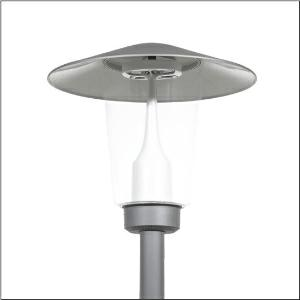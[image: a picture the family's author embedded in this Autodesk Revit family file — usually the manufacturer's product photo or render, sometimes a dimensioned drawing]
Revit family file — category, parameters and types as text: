
# Revit family: pilzleuchte_iq___p1_0a_5xa5235nf14hp_8191
name_source: partatom
category: Lighting Fixtures
units: mm (PartAtom-declared; Revit-internal decimal feet)

## family parameters
Cut with Voids When Loaded = No
Host = Face
Light Source = No
Part Type = Normal
Room Calculation Point = No
Round Connector Dimension = Use Diameter
Shared = No

## types (1)
- --- (1 x LED, 4250 lm, 33.6 W, 2700K)
    Apparent Load = 34 VA
    CIE Flux Codes = 35 64 90 96 100
    Color Rendering = 70
    Color Temperature = 2700K
    Default Elevation = 1800 mm
    Description = Mushroom Luminaire iQ, mast luminaire, Module 540 iQ-SR, primary light control with 3 zone facetted reflector, of plastic, silver coated, highly specular, structured, primary optical cover: cover, of PMMA, transparent, light distribution: P1.0a, light emission: direct distribution, primary light characteristic: strongly asymmetric, installation type: post-top, LED, High Power LED, rated luminous flux: 4.250lm, luminous efficacy: 127lm/W, light colour: 727, colour temperature: 2700K, control gear: ECG iQ, control: presetting dimming logarithmic, Street-Remote, Auto-Match, Temp-Guard, Lumen-Switch, Night-Set, Smart-Wire, Light-Fading, Desk-Remote (wireless, voltage-free reading and setting of iQ features in the workshop via application-optimized NFC function/RFID function), optimised constant luminous flux control (CLO 2.0), with terminal, 6-pole, max. 2.5mm², mains connection: 230..240V, AC, 50/60Hz, start of lifetime: 34W, end of service life: 36W, reduction: 15W, luminaire housing, upper part, of glass-fibre reinforced polyester, coated, Siteco® metallic grey (DB 702S), diameter: 650mm, height: 586mm, spigot size: d x l = 76 x 70mm (post-top) | with reducer (optional accessory) 60 x 70mm, post-top mast mounting element, of diecast aluminium, coated, Siteco® metallic grey (DB 702S), Module 540 iQ-SR, traffic white (RAL 9016), equipment: Power, protection rating (complete): IP65, insulation class (complete): insulation class II (safety insulation), certification: CE, ENEC, VDE, packaging unit: 1 piece

Light Distribution: P1.0a
    Height = 586 mm
    Lamp = 1 x LED
    Lamp Light Flux = 4250 lm
    Lamp Power = 33.6 W
    Lamp count = 1
    Length = 650 mm
    Luminous efficacy = 126 lm/W
    Manufacturer = Siteco
    ModVariant = No
    Model = 5XA5235NF14HP
    Number of Poles = 1
    OnlyDefault = Yes
    Power Factor = 1
    Product Name = Pilzleuchte iQ | P1.0a
    Product group = mast luminaire | pylon top
    ProductGroupID = 6100
    Protection Class = Protection class II
    Protection Degree = IP 65
    RLX_Detail_Level = 1
    RLX_Emergency_Light_Flux = 0 lm
    RLX_Emergency_Type = 0
    RLX_Emergency_Type_DB = No
    RlxData = <blob elided: 51913 chars, md5=ce1a9bcf>
    Socket = socket
    Standby Power = 0 W
    System Light Flux = 4250 lm
    System Power = 34 W
    Type Comments = factory setting: luminous flux: 100 % | dim-lin: 254 | 695 mA
    Type Image = l_1006077.jpg
    URL = http://relux.com
    VarID = @adj_102443
    Voltage = 0 V
    Weight = 0.00 kg
    Width = 0 mm  [stored 0 ft]

note: [stored X ft] marks values corroborated as IEEE doubles in the binary element streams (Revit-internal decimal feet)

## geometry (parser evidence)
native form markers: Blend x4, Sweep x12
no freeform markers — native parametric forms only
